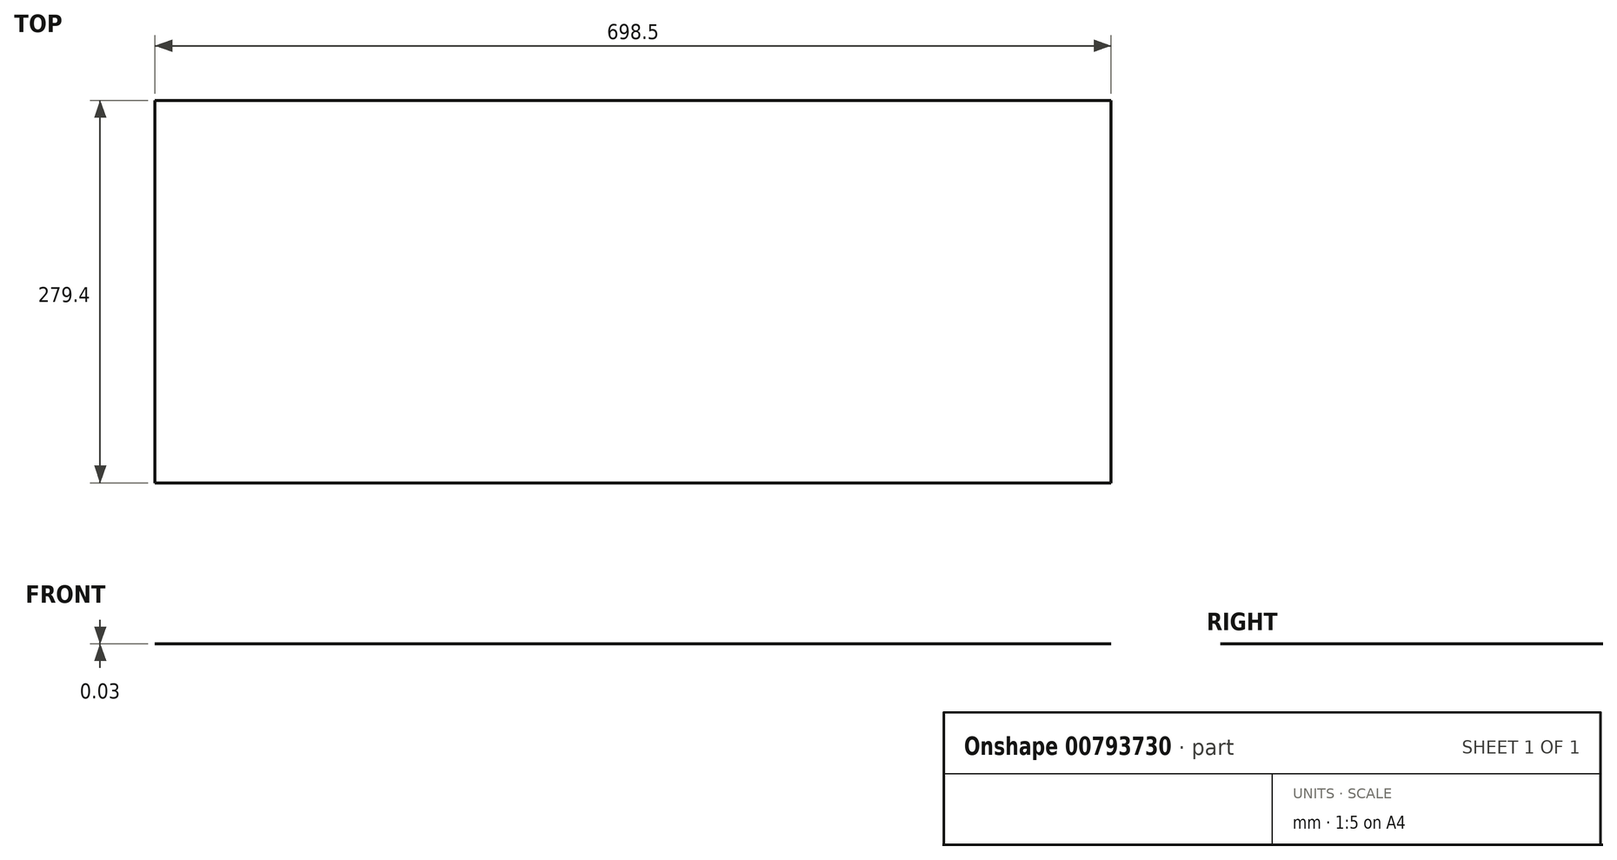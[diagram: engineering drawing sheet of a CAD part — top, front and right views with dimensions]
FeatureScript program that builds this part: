
annotation { "Feature Type Name" : "Feature", "Feature Type Description" : "" }
export const myFeature = defineFeature(function(context is Context, id is Id, definition is map)
    precondition{}
    {
        {
            var Q0;
            Q0=qCreatedBy(makeId("Top.planeOp"),FACE);
            var sketch = newSketch(context, id + "F0", { "sketchPlane" : qUnion([Q0])});
            skLineSegment(sketch, "E0.bottom", {"start": v(0, 0) * mm, "end": v(698.5, 0) * mm});
            skLineSegment(sketch, "E0.top", {"start": v(0, 279.4) * mm, "end": v(698.5, 279.4) * mm});
            skLineSegment(sketch, "E0.left", {"start": v(0, 0) * mm, "end": v(0, 279.4) * mm});
            skLineSegment(sketch, "E0.right", {"start": v(698.5, 0) * mm, "end": v(698.5, 279.4) * mm});
            skSolve(sketch);
        }
        {
            var Q0;
            Q0 = qSketchRegion(id + "F0", true);
            extrude(context, id + "F1", {"entities" : qUnion([Q0]), "depth" : 7 / 203.2 * mm, "offsetDistance" : 25.4 * mm});
        }
    });
